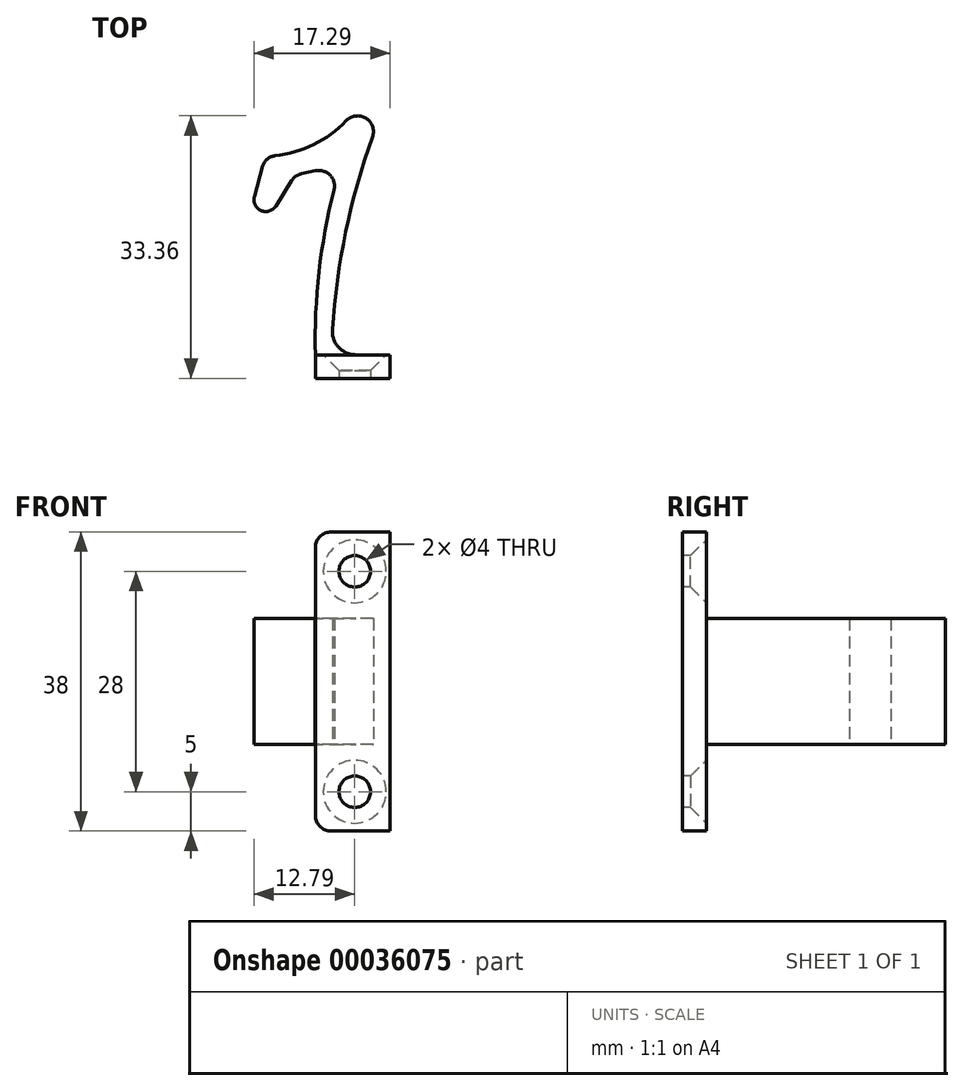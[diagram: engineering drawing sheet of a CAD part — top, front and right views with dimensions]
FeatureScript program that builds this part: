
annotation { "Feature Type Name" : "Feature", "Feature Type Description" : "" }
export const myFeature = defineFeature(function(context is Context, id is Id, definition is map)
    precondition{}
    {
        {
            var Q0;
            Q0=qCreatedBy(makeId("Top.planeOp"),FACE);
            var sketch = newSketch(context, id + "F0", { "sketchPlane" : qUnion([Q0])});
            skLineSegment(sketch, "E0", {"start": v(0, 33) * mm, "end": v(43.76, 33) * mm, "construction": true});
            skLineSegment(sketch, "E1", {"start": v(0, 3) * mm, "end": v(43.76, 3) * mm, "construction": true});
            skArc(sketch, "E2", {"start": v(7.25, 30.69) * mm, "mid": v(3.55, 17.05) * mm, "end": v(2, 3) * mm});
            skArc(sketch, "E3", {"start": v(2.36, 23.94) * mm, "mid": v(0.46, 13.55) * mm, "end": v(0, 3) * mm});
            skArc(sketch, "E4", {"start": v(-5.11, 28.3) * mm, "mid": v(-0.2, 29.7) * mm, "end": v(3.91, 32.74) * mm});
            skArc(sketch, "E5", {"start": v(7.25, 30.69) * mm, "mid": v(6.41, 33.06) * mm, "end": v(3.91, 32.74) * mm});
            skArc(sketch, "E6", {"start": v(2.36, 23.94) * mm, "mid": v(1.86, 25.82) * mm, "end": v(0, 26.38) * mm});
            skArc(sketch, "E7", {"start": v(-7.74, 23.1) * mm, "mid": v(-6.9, 21.33) * mm, "end": v(-5.02, 21.91) * mm});
            skLineSegment(sketch, "E8", {"start": v(-7.74, 23.1) * mm, "end": v(-6.69, 26.96) * mm});
            skLineSegment(sketch, "E9", {"start": v(-5.02, 21.91) * mm, "end": v(-2.58, 25.82) * mm});
            skLineSegment(sketch, "E10", {"start": v(-2.58, 25.82) * mm, "end": v(0, 26.38) * mm});
            skLineSegment(sketch, "E11", {"start": v(0, 3) * mm, "end": v(0, 0) * mm});
            skLineSegment(sketch, "E12", {"start": v(0, 0) * mm, "end": v(9.5, 0) * mm});
            skLineSegment(sketch, "E13", {"start": v(9.5, 0) * mm, "end": v(9.5, 3) * mm});
            skLineSegment(sketch, "E14", {"start": v(9.5, 3) * mm, "end": v(2, 3) * mm});
            skArc(sketch, "E15", {"start": v(-5.11, 28.3) * mm, "mid": v(-6.1, 27.87) * mm, "end": v(-6.69, 26.96) * mm});
            skSolve(sketch);
        }
        {
            var Q0;
            Q0=makeQuery(id+"F0.imprint","IMPRINT",FACE,{"disambiguationData":[TD([[makeQuery(id+"F0.imprint","IMPRINT",EDGE,{"derivedFrom":sQuery(id+"F0.wireOp",EDGE,"E2")}),-1.0]])]});
            extrude(context, id + "F1", {"entities" : qUnion([Q0]), "depth" : 16 * mm});
        }
        {
            var Q0;
            Q0=makeQuery(id+"F1.opExtrude","CAP_FACE",FACE,{"disambiguationData":[OSD([sQuery(id+"F0.wireOp",EDGE,"E2"),sQuery(id+"F0.wireOp",EDGE,"E3"),sQuery(id+"F0.wireOp",EDGE,"E4"),sQuery(id+"F0.wireOp",EDGE,"E5"),sQuery(id+"F0.wireOp",EDGE,"E6"),sQuery(id+"F0.wireOp",EDGE,"E7"),sQuery(id+"F0.wireOp",EDGE,"E8"),sQuery(id+"F0.wireOp",EDGE,"E9"),sQuery(id+"F0.wireOp",EDGE,"E10"),sQuery(id+"F0.wireOp",EDGE,"E11"),sQuery(id+"F0.wireOp",EDGE,"E12"),sQuery(id+"F0.wireOp",EDGE,"E13"),sQuery(id+"F0.wireOp",EDGE,"E14"),sQuery(id+"F0.wireOp",EDGE,"E15")])],"isStart":false});
            var sketch = newSketch(context, id + "F2", { "sketchPlane" : qUnion([Q0])});
            skLineSegment(sketch, "E16.bottom", {"start": v(9.5, 0) * mm, "end": v(0, 0) * mm});
            skLineSegment(sketch, "E16.top", {"start": v(9.5, 3) * mm, "end": v(0, 3) * mm});
            skLineSegment(sketch, "E16.left", {"start": v(9.5, 0) * mm, "end": v(9.5, 3) * mm});
            skLineSegment(sketch, "E16.right", {"start": v(0, 0) * mm, "end": v(0, 3) * mm});
            skSolve(sketch);
        }
        {
            var Q0;
            Q0 = qSketchRegion(id + "F2", true);
            extrude(context, id + "F3", {"entities" : qUnion([Q0]), "depth" : 11 * mm});
        }
        {
            var Q0;
            Q0=qCreatedBy(makeId("Top.planeOp"),FACE);
            cPlane(context, id + "F4", {"entities" : qUnion([Q0]), "cplaneType" : CPlaneType.OFFSET, "offset" : 8 * mm, "width" : 150 * mm, "height" : 150 * mm});
        }
        {
            var Q0;
            Q0=makeQuery(id+"F3.opExtrude","SWEPT_FACE",FACE,{"disambiguationData":[OSD([sQuery(id+"F2.wireOp",EDGE,"E16.top")])]});
            var sketch = newSketch(context, id + "F5", { "sketchPlane" : qUnion([Q0])});
            skPoint(sketch, "E17", {"position": v(-5, 22) * mm});
            skSolve(sketch);
        }
        {
            var Q0;
            Q0=sQuery(id+"F5.wireOp",VERTEX,"E17");
            var Q1;
            Q1=makeQuery(id+"F3.opExtrude","SWEPT_BODY",BODY,{"disambiguationData":[OSD([sQuery(id+"F2.wireOp",EDGE,"E16.bottom"),sQuery(id+"F2.wireOp",EDGE,"E16.top"),sQuery(id+"F2.wireOp",EDGE,"E16.left"),sQuery(id+"F2.wireOp",EDGE,"E16.right")])]});
            hole(context, id + "F6", {"style" : HoleStyle.C_SINK, "holeDiameter" : 4 * mm, "cSinkDiameter" : 8 * mm, "endStyle" : HoleEndStyle.THROUGH, "locations" : qUnion([Q0]), "scope" : qUnion([Q1]), "cSinkAngle" : 90 * degree});
        }
        {
            var Q0;
            Q0=makeQuery(id+"F3.opExtrude","SWEPT_BODY",BODY,{"disambiguationData":[OSD([sQuery(id+"F2.wireOp",EDGE,"E16.bottom"),sQuery(id+"F2.wireOp",EDGE,"E16.top"),sQuery(id+"F2.wireOp",EDGE,"E16.left"),sQuery(id+"F2.wireOp",EDGE,"E16.right")])]});
            var Q1;
            Q1=qCreatedBy(id+"F4.planeOp",FACE);
            mirror(context, id + "F7", {"operationType" : NewBodyOperationType.ADD, "entities" : qUnion([Q0]), "mirrorPlane" : qUnion([Q1])});
        }
        {
            var Q0;
            Q0=makeQuery(id+"F3.opExtrude","CAP_EDGE",EDGE,{"disambiguationData":[OSD([sQuery(id+"F2.wireOp",EDGE,"E16.right")])],"isStart":false});
            var Q1;
            Q1=makeQuery(id+"F7.opPattern","COPY",EDGE,{"derivedFrom":makeQuery(id+"F3.opExtrude","CAP_EDGE",EDGE,{"disambiguationData":[OSD([sQuery(id+"F2.wireOp",EDGE,"E16.right")])],"isStart":false}),"instanceName":"1"});
            fillet(context, id + "F8", {"entities" : qUnion([Q0, Q1]), "radius" : 2 * mm, "tangentPropagation" : true, "allowEdgeOverflow" : false});
        }
        {
            var Q0;
            Q0=makeQuery(id+"F1.opExtrude","SWEPT_EDGE",EDGE,{"disambiguationData":[OSD([sQuery(id+"F0.wireOp",EDGE,"E2"),sQuery(id+"F0.wireOp",EDGE,"E14")])]});
            fillet(context, id + "F9", {"entities" : qUnion([Q0]), "radius" : 3 * mm, "tangentPropagation" : true, "allowEdgeOverflow" : false});
        }
        {
            var Q0;
            Q0=makeQuery(id+"F1.opExtrude","SWEPT_EDGE",EDGE,{"disambiguationData":[OSD([sQuery(id+"F0.wireOp",EDGE,"E9"),sQuery(id+"F0.wireOp",EDGE,"E10")])]});
            fillet(context, id + "F10", {"entities" : qUnion([Q0]), "radius" : 2 * mm, "tangentPropagation" : true, "allowEdgeOverflow" : false});
        }
    });
